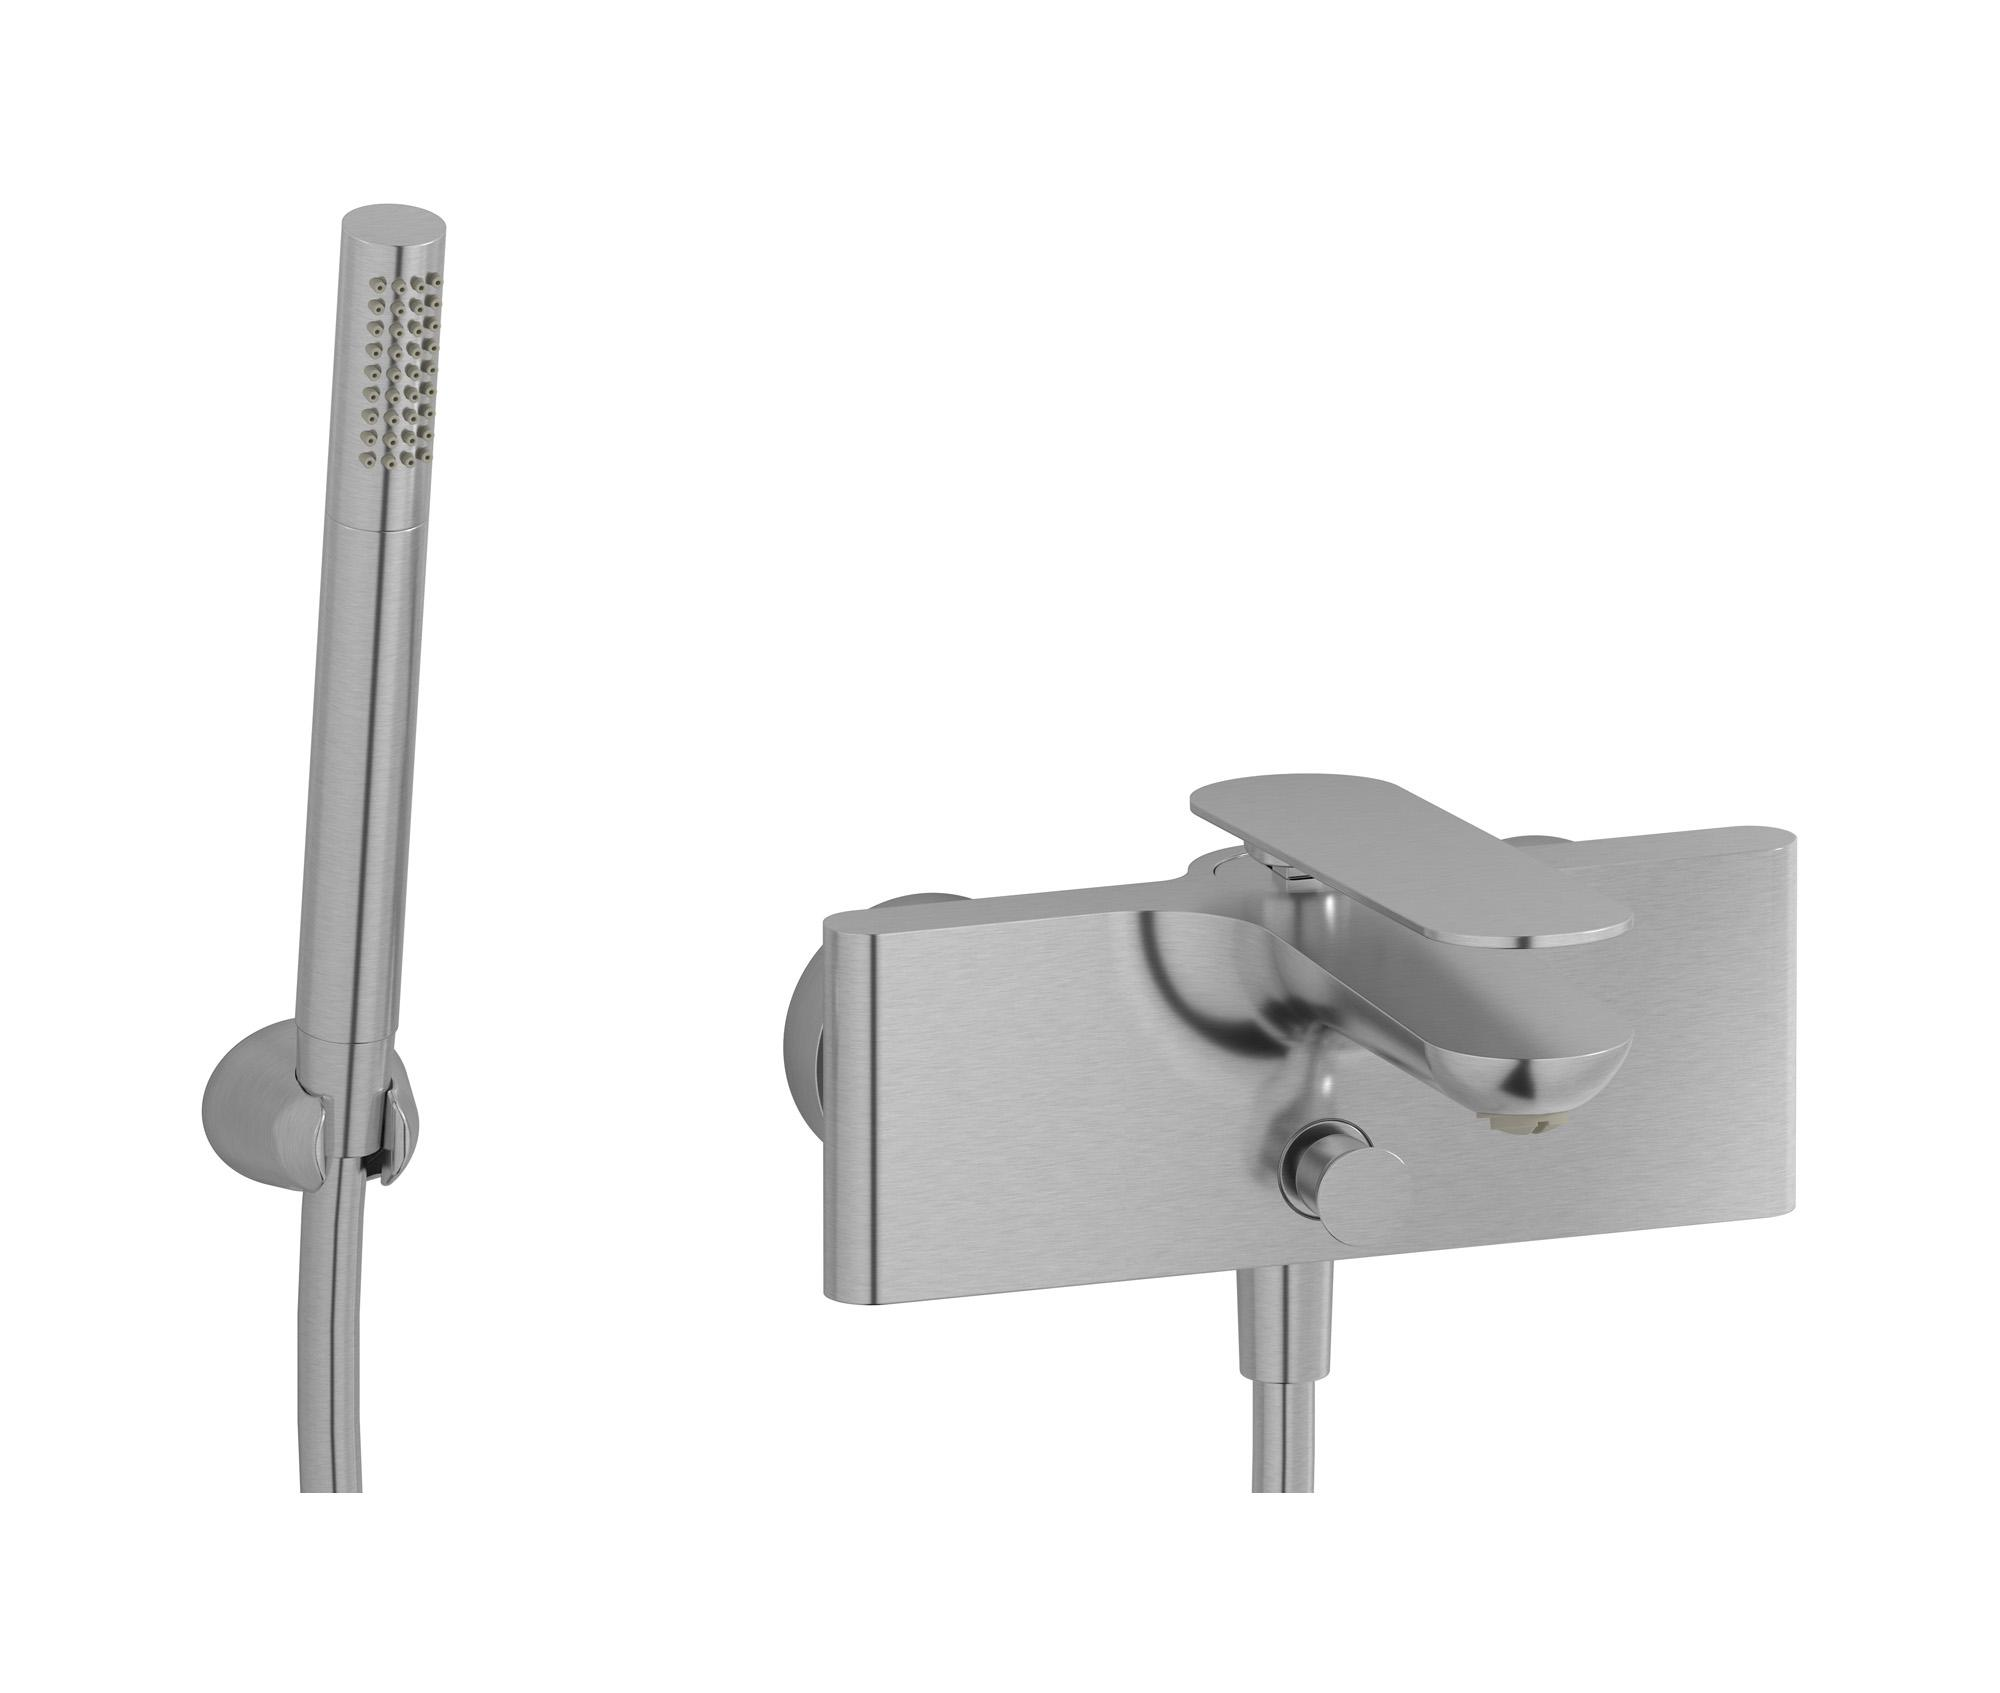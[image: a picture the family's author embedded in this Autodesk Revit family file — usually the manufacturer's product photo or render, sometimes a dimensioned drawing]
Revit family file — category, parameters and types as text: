
# Revit family: K2250
name_source: partatom
category: Apparecchi idraulici
units: mm (PartAtom-declared; Revit-internal decimal feet)

## family parameters
Basato su piano di lavoro = No
Condiviso = No
Mantieni orientamento annotazione = No
Numero OmniClass = 23.45.55.17
Punto di calcolo locali = No
Quota connettore circolare = Usa diametro
Sempre verticale = Sì
Taglio con vuoti quando caricato = No
Tipo di parte = Normale
Titolo OmniClass = Mixing Faucets

## types (9) — shared parameters
Cold water inlet = 10 mm  [stored 0.0328084 ft]
Commenti sul tipo = Bath filler
Connessione CW = No
Connessione HW = No
Connessione di scarico = No
Connessione di ventilazione = No
Descrizione = Wall mounted bath filler complete with shower kit
Hot water inlet = 10 mm  [stored 0.0328084 ft]
Produttore = IB Rubinetterie S.p.A.
URL = https://www.weareib.it
zero-valued in all types: Prospetto di default

## per-type parameters (varying)
| type | Finishes surface | Immagine tipo | Modello |
| Chrome | IB_Chrome | K2250CC.jpg | K2250CC |
| Platinum | IB_Platinum | K2250PL.jpg | K2250PL |
| Matt black | IB_matt black | K2250NP.jpg | K2250NP |
| Matt white | IB_matt white | K2250BO.jpg | K2250BO |
| Pale gold | IB_Pale gold | K2250II.jpg | K2250II |
| Brushed pale gold | IB_brushed pale gold | K2250IS.jpg | K2250IS |
| Rose gold | IB_Rose gold | K2250RS.jpg | K2250RS |
| Gold | IB_gold | K2250OO.jpg | K2250OO |
| Brushed nickel | IB_Brushed nickel | K2250SS.jpg | K2250SS |

note: [stored X ft] marks values corroborated as IEEE doubles in the binary element streams (Revit-internal decimal feet)
